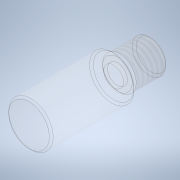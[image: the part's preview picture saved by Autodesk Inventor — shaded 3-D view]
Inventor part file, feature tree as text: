
AUTODESK INVENTOR PART (.ipt)
format: ipt  version: 2021.3 (Build 253353000, 353)  size: 146,944 bytes
history: native  units: mm
features: revolve x1, fillet x1, thread x1, sketch x1
ambient origin geometry x8: Origin, YZ Plane, XZ Plane, XY Plane, X Axis, Y Axis, Z Axis, Center Point
bodies: Volumenkörper1 (feature_tree)
feature tree (4):
  revolve  "Umdrehung1"
  fillet  "Rundung1"  Radius=5.775mm
  thread  "Gewinde1"  [1 undecoded]
  sketch  "Skizze1"  dims[d2=3.7mm d3=1.0mm d4=8.7mm d5=4.35mm d6=90.0deg d7=0.5mm d9=7.7mm d10=0.0mm]
note: 1 required parameter value undecoded (feature->parameter linkage not recoverable at this tier; creation-order binding heuristic only, values carry confidence <= 0.55)
